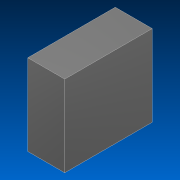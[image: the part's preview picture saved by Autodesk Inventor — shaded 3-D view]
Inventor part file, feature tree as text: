
AUTODESK INVENTOR PART (.ipt)
format: ipt  version: 2022.2 (Build 262287000, 287)  size: 79,872 bytes
history: native  units: in
note: dims shown in document units (in); Inventor stores cm internally (conversion verified against a paired STEP export)
features: extrude x1, sketch x1
ambient origin geometry x8: Origin, YZ Plane, XZ Plane, XY Plane, X Axis, Y Axis, Z Axis, Center Point
bodies: Solid1 (feature_tree)
feature tree (2):
  extrude  "Extrusion1"  Depth=6.58in
  sketch  "Sketch1"  dims[d0=3.0in d1=6.58in d2=7.1in d3=0.0in]
